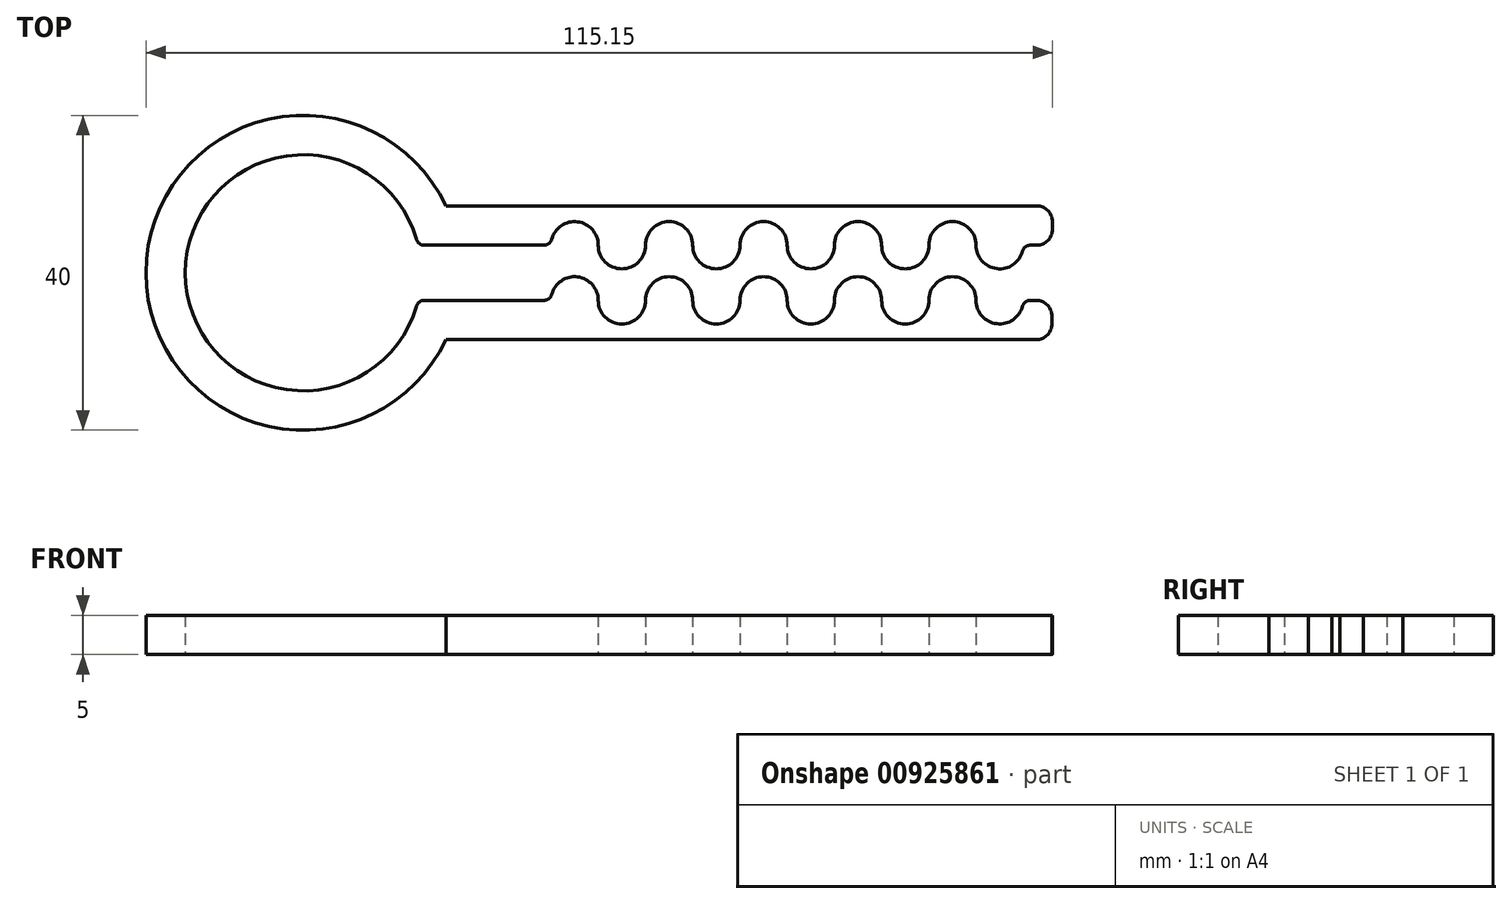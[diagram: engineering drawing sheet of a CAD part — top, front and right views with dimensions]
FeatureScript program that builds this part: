
annotation { "Feature Type Name" : "Feature", "Feature Type Description" : "" }
export const myFeature = defineFeature(function(context is Context, id is Id, definition is map)
    precondition{}
    {
        {
            var Q0;
            Q0=qCreatedBy(makeId("Top.planeOp"),FACE);
            var sketch = newSketch(context, id + "F0", { "sketchPlane" : qUnion([Q0])});
            skArc(sketch, "E0", {"start": v(-32.6, 7.22) * mm, "mid": v(-35.6, 10.22) * mm, "end": v(-38.6, 7.22) * mm});
            skArc(sketch, "E1", {"start": v(-32.6, 7.22) * mm, "mid": v(-29.6, 4.22) * mm, "end": v(-26.6, 7.22) * mm});
            skArc(sketch, "E2", {"start": v(-20.6, 7.22) * mm, "mid": v(-23.6, 10.22) * mm, "end": v(-26.6, 7.22) * mm});
            skArc(sketch, "E3", {"start": v(-20.6, 7.22) * mm, "mid": v(-17.6, 4.22) * mm, "end": v(-14.6, 7.22) * mm});
            skArc(sketch, "E4", {"start": v(-8.6, 7.22) * mm, "mid": v(-11.6, 10.22) * mm, "end": v(-14.6, 7.22) * mm});
            skArc(sketch, "E5", {"start": v(-8.6, 7.22) * mm, "mid": v(-5.6, 4.22) * mm, "end": v(-2.6, 7.22) * mm});
            skArc(sketch, "E6", {"start": v(3.4, 7.22) * mm, "mid": v(0.4, 10.22) * mm, "end": v(-2.6, 7.22) * mm});
            skArc(sketch, "E7", {"start": v(3.4, 7.22) * mm, "mid": v(6.4, 4.22) * mm, "end": v(9.4, 7.22) * mm});
            skArc(sketch, "E8", {"start": v(15.4, 7.22) * mm, "mid": v(12.4, 10.22) * mm, "end": v(9.4, 7.22) * mm});
            skArc(sketch, "E9", {"start": v(15.4, 7.22) * mm, "mid": v(18.4, 4.22) * mm, "end": v(21.4, 7.22) * mm});
            skArc(sketch, "E10", {"start": v(-32.6, 0.22) * mm, "mid": v(-35.6, 3.22) * mm, "end": v(-38.6, 0.22) * mm});
            skArc(sketch, "E11", {"start": v(-32.6, 0.22) * mm, "mid": v(-29.6, -2.78) * mm, "end": v(-26.6, 0.22) * mm});
            skArc(sketch, "E12", {"start": v(-20.6, 0.22) * mm, "mid": v(-23.6, 3.22) * mm, "end": v(-26.6, 0.22) * mm});
            skArc(sketch, "E13", {"start": v(-20.6, 0.22) * mm, "mid": v(-17.6, -2.78) * mm, "end": v(-14.6, 0.22) * mm});
            skArc(sketch, "E14", {"start": v(-8.6, 0.22) * mm, "mid": v(-11.6, 3.22) * mm, "end": v(-14.6, 0.22) * mm});
            skArc(sketch, "E15", {"start": v(-8.6, 0.22) * mm, "mid": v(-5.6, -2.78) * mm, "end": v(-2.6, 0.22) * mm});
            skArc(sketch, "E16", {"start": v(3.4, 0.22) * mm, "mid": v(0.4, 3.22) * mm, "end": v(-2.6, 0.22) * mm});
            skArc(sketch, "E17", {"start": v(3.4, 0.22) * mm, "mid": v(6.4, -2.78) * mm, "end": v(9.4, 0.22) * mm});
            skArc(sketch, "E18", {"start": v(15.4, 0.22) * mm, "mid": v(12.4, 3.22) * mm, "end": v(9.4, 0.22) * mm});
            skArc(sketch, "E19", {"start": v(15.4, 0.22) * mm, "mid": v(18.4, -2.78) * mm, "end": v(21.4, 0.22) * mm});
            skLineSegment(sketch, "E20", {"start": v(25.1, 9.22) * mm, "end": v(25.1, 10.22) * mm});
            skLineSegment(sketch, "E21", {"start": v(23.1, 12.22) * mm, "end": v(-51.95, 12.22) * mm});
            skLineSegment(sketch, "E22", {"start": v(21.4, 0.22) * mm, "end": v(23.04, 0.22) * mm});
            skLineSegment(sketch, "E23", {"start": v(25.04, -1.78) * mm, "end": v(25.04, -2.78) * mm});
            skLineSegment(sketch, "E24", {"start": v(23.04, -4.78) * mm, "end": v(-51.95, -4.78) * mm});
            skArc(sketch, "E25", {"start": v(-51.95, 12.22) * mm, "mid": v(-90.05, 3.72) * mm, "end": v(-51.95, -4.78) * mm});
            skLineSegment(sketch, "E26", {"start": v(-38.6, 7.22) * mm, "end": v(-55.46, 7.22) * mm});
            skLineSegment(sketch, "E27", {"start": v(-38.6, 0.22) * mm, "end": v(-55.46, 0.22) * mm});
            skArc(sketch, "E28", {"start": v(-55.46, 7.22) * mm, "mid": v(-85.05, 3.72) * mm, "end": v(-55.46, 0.22) * mm});
            skPoint(sketch, "E29.visualSharp", {"position": v(25.1, 12.22) * mm});
            skArc(sketch, "E29.filletArc", {"start": v(25.1, 10.22) * mm, "mid": v(24.52, 11.63) * mm, "end": v(23.1, 12.22) * mm});
            skPoint(sketch, "E30.visualSharp", {"position": v(25.04, 0.22) * mm});
            skArc(sketch, "E30.filletArc", {"start": v(25.04, -1.78) * mm, "mid": v(24.45, -0.37) * mm, "end": v(23.04, 0.22) * mm});
            skPoint(sketch, "E31.visualSharp", {"position": v(25.04, -4.78) * mm});
            skArc(sketch, "E31.filletArc", {"start": v(23.04, -4.78) * mm, "mid": v(24.45, -4.2) * mm, "end": v(25.04, -2.78) * mm});
            skLineSegment(sketch, "E32", {"start": v(21.4, 7.22) * mm, "end": v(23.1, 7.22) * mm});
            skPoint(sketch, "E33.visualSharp", {"position": v(25.1, 7.22) * mm});
            skArc(sketch, "E33.filletArc", {"start": v(23.1, 7.22) * mm, "mid": v(24.52, 7.8) * mm, "end": v(25.1, 9.22) * mm});
            skSolve(sketch);
        }
        {
            var Q0;
            Q0=makeQuery(id+"F0.imprint","IMPRINT",FACE,{"disambiguationData":[TD([[makeQuery(id+"F0.imprint","IMPRINT",EDGE,{"derivedFrom":sQuery(id+"F0.wireOp",EDGE,"E0")}),-1.0]])]});
            extrude(context, id + "F1", {"entities" : qUnion([Q0]), "depth" : 5 * mm, "offsetDistance" : 25 * mm});
        }
        {
            var Q0;
            Q0=makeQuery(id+"F1.opExtrude","SWEPT_EDGE",EDGE,{"disambiguationData":[OSD([sQuery(id+"F0.wireOp",EDGE,"E26"),sQuery(id+"F0.wireOp",EDGE,"E28")])]});
            var Q1;
            Q1=makeQuery(id+"F1.opExtrude","SWEPT_EDGE",EDGE,{"disambiguationData":[OSD([sQuery(id+"F0.wireOp",EDGE,"E0"),sQuery(id+"F0.wireOp",EDGE,"E26")])]});
            var Q2;
            Q2=makeQuery(id+"F1.opExtrude","SWEPT_EDGE",EDGE,{"disambiguationData":[OSD([sQuery(id+"F0.wireOp",EDGE,"E10"),sQuery(id+"F0.wireOp",EDGE,"E27")])]});
            var Q3;
            Q3=makeQuery(id+"F1.opExtrude","SWEPT_EDGE",EDGE,{"disambiguationData":[OSD([sQuery(id+"F0.wireOp",EDGE,"E27"),sQuery(id+"F0.wireOp",EDGE,"E28")])]});
            var Q4;
            Q4=makeQuery(id+"F1.opExtrude","SWEPT_EDGE",EDGE,{"disambiguationData":[OSD([sQuery(id+"F0.wireOp",EDGE,"E9"),sQuery(id+"F0.wireOp",EDGE,"9a836034-344a-4ad8-a634-5ead2c854508.filletArc")])]});
            var Q5;
            Q5=makeQuery(id+"F1.opExtrude","SWEPT_EDGE",EDGE,{"disambiguationData":[OSD([sQuery(id+"F0.wireOp",EDGE,"E19"),sQuery(id+"F0.wireOp",EDGE,"E30.filletArc")])]});
            fillet(context, id + "F2", {"entities" : qUnion([Q0, Q1, Q2, Q3, Q4, Q5]), "radius" : 1 * mm, "tangentPropagation" : true, "allowEdgeOverflow" : false});
        }
    });
